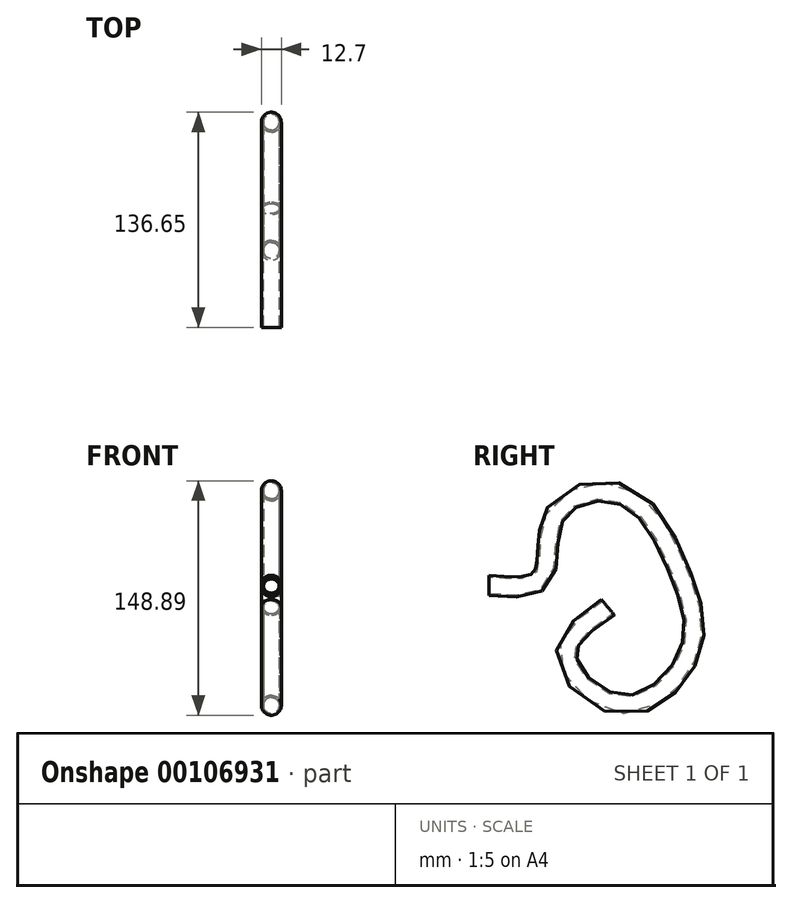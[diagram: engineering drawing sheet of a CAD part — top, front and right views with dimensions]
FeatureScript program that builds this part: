
annotation { "Feature Type Name" : "Feature", "Feature Type Description" : "" }
export const myFeature = defineFeature(function(context is Context, id is Id, definition is map)
    precondition{}
    {
        {
            var Q0;
            Q0=qCreatedBy(makeId("Front.planeOp"),FACE);
            var sketch = newSketch(context, id + "F0", { "sketchPlane" : qUnion([Q0])});
            skCircle(sketch, "E0", {"center": v(0, 0) * mm, "radius": 6.35 * mm});
            skSolve(sketch);
        }
        {
            var Q0;
            Q0=qCreatedBy(makeId("Right.planeOp"),FACE);
            var sketch = newSketch(context, id + "F1", { "sketchPlane" : qUnion([Q0])});
            skFitSpline(sketch, "E1", {"points": [v(0, 0) * mm, v(34, 5.04) * mm, v(41.67, 44.72) * mm, v(85.09, 57.6) * mm, v(120.87, 9.03) * mm, v(128.03, -41.42) * mm, v(86.2, -76.3) * mm, v(49.02, -44.87) * mm, v(75.55, -14.06) * mm], "startDerivative": vector(401.35, -37.15) * mm, "endDerivative": vector(352.73, 236.65) * mm});
            skSolve(sketch);
        }
        {
            var Q0;
            Q0=makeQuery(id+"F0.imprint","IMPRINT",FACE,{"disambiguationData":[TD([[makeQuery(id+"F0.imprint","IMPRINT",EDGE,{"derivedFrom":sQuery(id+"F0.wireOp",EDGE,"E0")}),1.0]])]});
            var Q1;
            Q1=sQuery(id+"F1.wireOp",EDGE,"E1");
            sweep(context, id + "F2", {"profiles" : qUnion([Q0]), "path" : qUnion([Q1])});
        }
        {
            var Q0;
            Q0=makeQuery(id+"F2.opSweep","CAP_FACE",FACE,{"disambiguationData":[OSD([sQuery(id+"F0.wireOp",EDGE,"E0"),sQuery(id+"F1.wireOp",VERTEX,"E1.start")])],"isStart":true});
            var sketch = newSketch(context, id + "F3", { "sketchPlane" : qUnion([Q0])});
            skCircle(sketch, "E2", {"center": v(0, 0) * mm, "radius": 5.08 * mm});
            skSolve(sketch);
        }
        {
            var Q0;
            Q0=makeQuery(id+"F3.imprint","IMPRINT",FACE,{"disambiguationData":[TD([[makeQuery(id+"F3.imprint","IMPRINT",EDGE,{"derivedFrom":sQuery(id+"F3.wireOp",EDGE,"E2")}),1.0]])]});
            var Q1;
            Q1 = qConstructionFilter(qBodyType(qCreatedBy(id + "F1" ,EDGE), BodyType.WIRE), ConstructionObject.NO);
            sweep(context, id + "F4", {"operationType" : NewBodyOperationType.REMOVE, "profiles" : qUnion([Q0]), "path" : qUnion([Q1])});
        }
    });
